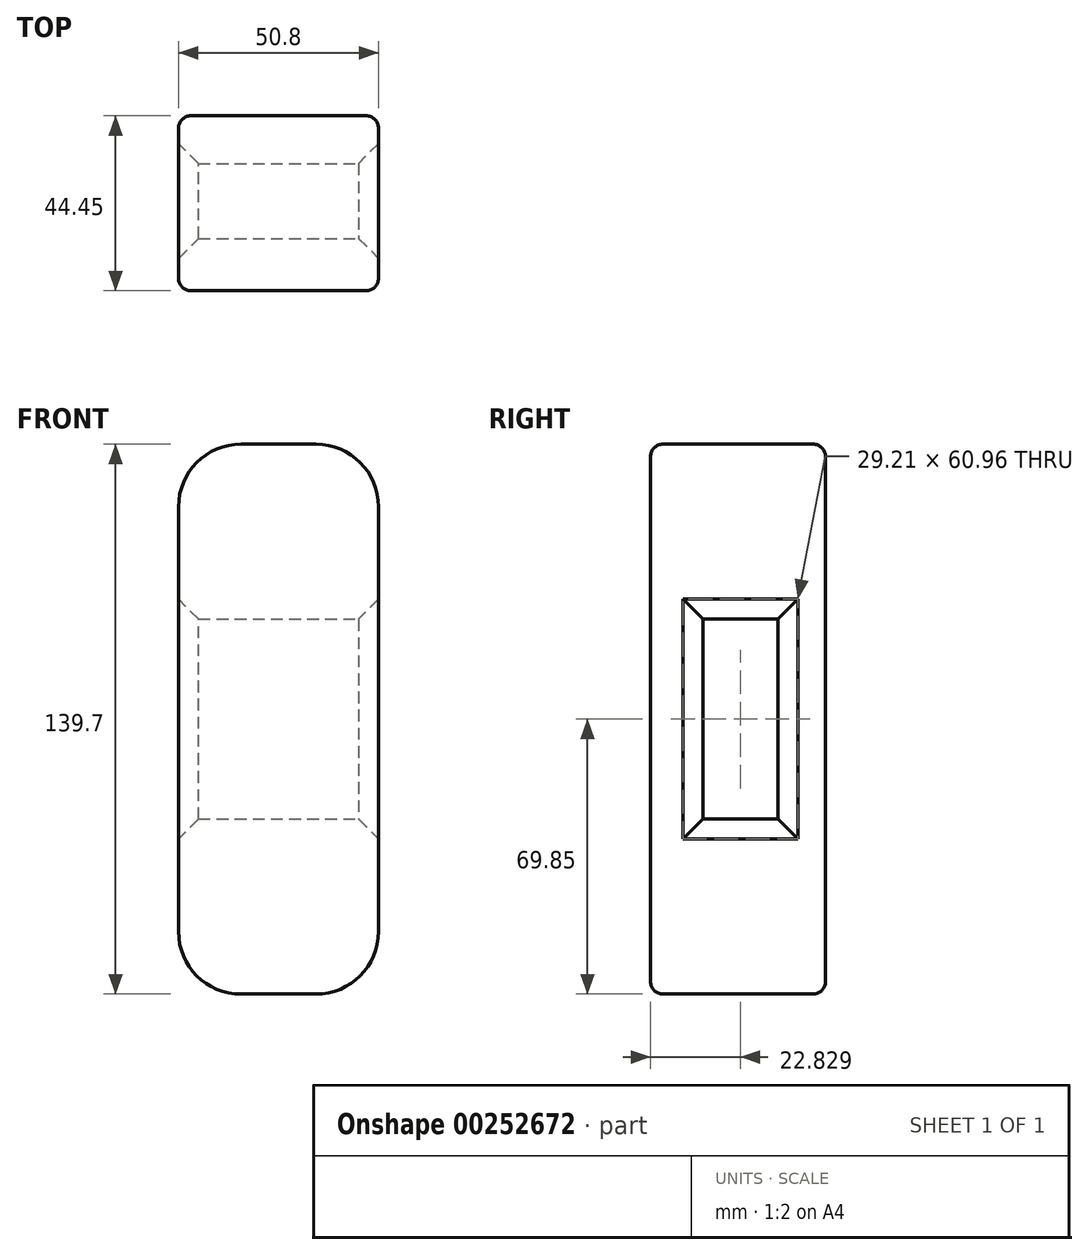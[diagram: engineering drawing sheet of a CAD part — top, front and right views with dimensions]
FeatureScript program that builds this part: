
annotation { "Feature Type Name" : "Feature", "Feature Type Description" : "" }
export const myFeature = defineFeature(function(context is Context, id is Id, definition is map)
    precondition{}
    {
        {
            var Q0;
            Q0=qCreatedBy(makeId("Front.planeOp"),FACE);
            var sketch = newSketch(context, id + "F0", { "sketchPlane" : qUnion([Q0])});
            skLineSegment(sketch, "E0.bottom", {"start": v(-9.52, 69.85) * mm, "end": v(9.53, 69.85) * mm});
            skLineSegment(sketch, "E0.top", {"start": v(-9.53, -69.85) * mm, "end": v(9.52, -69.85) * mm});
            skLineSegment(sketch, "E0.left", {"start": v(-25.4, 53.98) * mm, "end": v(-25.4, -53.97) * mm});
            skLineSegment(sketch, "E0.right", {"start": v(25.4, 53.98) * mm, "end": v(25.4, -53.97) * mm});
            skPoint(sketch, "E0.middle", {"position": v(0, 0) * mm});
            skPoint(sketch, "E1.visualSharp", {"position": v(-25.4, 69.85) * mm});
            skArc(sketch, "E1.filletArc", {"start": v(-9.52, 69.85) * mm, "mid": v(-20.75, 65.2) * mm, "end": v(-25.4, 53.98) * mm});
            skPoint(sketch, "E2.visualSharp", {"position": v(25.4, 69.85) * mm});
            skArc(sketch, "E2.filletArc", {"start": v(25.4, 53.98) * mm, "mid": v(20.75, 65.2) * mm, "end": v(9.53, 69.85) * mm});
            skPoint(sketch, "E3.visualSharp", {"position": v(25.4, -69.85) * mm});
            skArc(sketch, "E3.filletArc", {"start": v(9.52, -69.85) * mm, "mid": v(20.75, -65.2) * mm, "end": v(25.4, -53.97) * mm});
            skPoint(sketch, "E4.visualSharp", {"position": v(-25.4, -69.85) * mm});
            skArc(sketch, "E4.filletArc", {"start": v(-25.4, -53.97) * mm, "mid": v(-20.75, -65.2) * mm, "end": v(-9.53, -69.85) * mm});
            skSolve(sketch);
        }
        {
            var Q0;
            Q0=makeQuery(id+"F0.imprint","IMPRINT",FACE,{"disambiguationData":[TD([[makeQuery(id+"F0.imprint","IMPRINT",EDGE,{"derivedFrom":sQuery(id+"F0.wireOp",EDGE,"E0.bottom")}),-1.0]])]});
            extrude(context, id + "F1", {"entities" : qUnion([Q0]), "depth" : 44.45 * mm});
        }
        {
            var Q0;
            Q0=qCreatedBy(makeId("Right.planeOp"),FACE);
            var sketch = newSketch(context, id + "F2", { "sketchPlane" : qUnion([Q0])});
            skLineSegment(sketch, "E5.bottom", {"start": v(-31.15, 25.4) * mm, "end": v(-12.1, 25.4) * mm});
            skLineSegment(sketch, "E5.top", {"start": v(-31.15, -25.4) * mm, "end": v(-12.1, -25.4) * mm});
            skLineSegment(sketch, "E5.left", {"start": v(-31.15, 25.4) * mm, "end": v(-31.15, -25.4) * mm});
            skLineSegment(sketch, "E5.right", {"start": v(-12.1, 25.4) * mm, "end": v(-12.1, -25.4) * mm});
            skPoint(sketch, "E5.middle", {"position": v(-21.62, 0) * mm});
            skSolve(sketch);
        }
        {
            var Q0;
            Q0=makeQuery(id+"F1.opExtrude","CAP_EDGE",EDGE,{"disambiguationData":[OSD([sQuery(id+"F0.wireOp",EDGE,"E0.left")])],"isStart":false});
            var Q1;
            Q1=makeQuery(id+"F1.opExtrude","SWEPT_FACE",FACE,{"disambiguationData":[OSD([sQuery(id+"F0.wireOp",EDGE,"E0.left")])]});
            fillet(context, id + "F3", {"entities" : qUnion([Q0, Q1]), "radius" : 3.17 * mm, "tangentPropagation" : true, "allowEdgeOverflow" : false});
        }
        {
            var Q0;
            Q0 = qSketchRegion(id + "F2", true);
            extrude(context, id + "F4", {"entities" : qUnion([Q0]), "operationType" : NewBodyOperationType.REMOVE, "endBound" : BoundingType.THROUGH_ALL, "oppositeDirection" : true, "depth" : 25.4 * mm});
        }
        {
            var Q0;
            Q0 = qSketchRegion(id + "F2", true);
            extrude(context, id + "F5", {"entities" : qUnion([Q0]), "operationType" : NewBodyOperationType.REMOVE, "endBound" : BoundingType.THROUGH_ALL, "depth" : 25.4 * mm});
        }
        {
            var Q0;
            Q0=makeQuery(id+"F4.boolean.opBoolean","INTERSECT",EDGE,{"derivedFrom":[makeQuery(id+"F1.opExtrude","SWEPT_FACE",FACE,{"disambiguationData":[OSD([sQuery(id+"F0.wireOp",EDGE,"E0.left")])]}),makeQuery(id+"F4.opExtrude","SWEPT_FACE",FACE,{"disambiguationData":[OSD([sQuery(id+"F2.wireOp",EDGE,"E5.bottom")])]})]});
            var Q1;
            Q1=makeQuery(id+"F4.boolean.opBoolean","INTERSECT",EDGE,{"derivedFrom":[makeQuery(id+"F1.opExtrude","SWEPT_FACE",FACE,{"disambiguationData":[OSD([sQuery(id+"F0.wireOp",EDGE,"E0.left")])]}),makeQuery(id+"F4.opExtrude","SWEPT_FACE",FACE,{"disambiguationData":[OSD([sQuery(id+"F2.wireOp",EDGE,"E5.right")])]})]});
            var Q2;
            Q2=makeQuery(id+"F4.boolean.opBoolean","INTERSECT",EDGE,{"derivedFrom":[makeQuery(id+"F1.opExtrude","SWEPT_FACE",FACE,{"disambiguationData":[OSD([sQuery(id+"F0.wireOp",EDGE,"E0.left")])]}),makeQuery(id+"F4.opExtrude","SWEPT_FACE",FACE,{"disambiguationData":[OSD([sQuery(id+"F2.wireOp",EDGE,"E5.left")])]})]});
            var Q3;
            Q3=makeQuery(id+"F4.boolean.opBoolean","INTERSECT",EDGE,{"derivedFrom":[makeQuery(id+"F1.opExtrude","SWEPT_FACE",FACE,{"disambiguationData":[OSD([sQuery(id+"F0.wireOp",EDGE,"E0.left")])]}),makeQuery(id+"F4.opExtrude","SWEPT_FACE",FACE,{"disambiguationData":[OSD([sQuery(id+"F2.wireOp",EDGE,"E5.top")])]})]});
            chamfer(context, id + "F6", {"entities" : qUnion([Q0, Q1, Q2, Q3]), "width" : 5.08 * mm, "tangentPropagation" : true});
        }
        {
            var Q0;
            Q0=makeQuery(id+"F5.boolean.opBoolean","INTERSECT",EDGE,{"derivedFrom":[makeQuery(id+"F1.opExtrude","SWEPT_FACE",FACE,{"disambiguationData":[OSD([sQuery(id+"F0.wireOp",EDGE,"E0.right")])]}),makeQuery(id+"F5.opExtrude","SWEPT_FACE",FACE,{"disambiguationData":[OSD([sQuery(id+"F2.wireOp",EDGE,"E5.bottom")])]})]});
            var Q1;
            Q1=makeQuery(id+"F5.boolean.opBoolean","INTERSECT",EDGE,{"derivedFrom":[makeQuery(id+"F1.opExtrude","SWEPT_FACE",FACE,{"disambiguationData":[OSD([sQuery(id+"F0.wireOp",EDGE,"E0.right")])]}),makeQuery(id+"F5.opExtrude","SWEPT_FACE",FACE,{"disambiguationData":[OSD([sQuery(id+"F2.wireOp",EDGE,"E5.left")])]})]});
            var Q2;
            Q2=makeQuery(id+"F5.boolean.opBoolean","INTERSECT",EDGE,{"derivedFrom":[makeQuery(id+"F1.opExtrude","SWEPT_FACE",FACE,{"disambiguationData":[OSD([sQuery(id+"F0.wireOp",EDGE,"E0.right")])]}),makeQuery(id+"F5.opExtrude","SWEPT_FACE",FACE,{"disambiguationData":[OSD([sQuery(id+"F2.wireOp",EDGE,"E5.right")])]})]});
            var Q3;
            Q3=makeQuery(id+"F5.boolean.opBoolean","INTERSECT",EDGE,{"derivedFrom":[makeQuery(id+"F1.opExtrude","SWEPT_FACE",FACE,{"disambiguationData":[OSD([sQuery(id+"F0.wireOp",EDGE,"E0.right")])]}),makeQuery(id+"F5.opExtrude","SWEPT_FACE",FACE,{"disambiguationData":[OSD([sQuery(id+"F2.wireOp",EDGE,"E5.top")])]})]});
            chamfer(context, id + "F7", {"entities" : qUnion([Q0, Q1, Q2, Q3]), "width" : 5.08 * mm, "tangentPropagation" : true});
        }
    });
